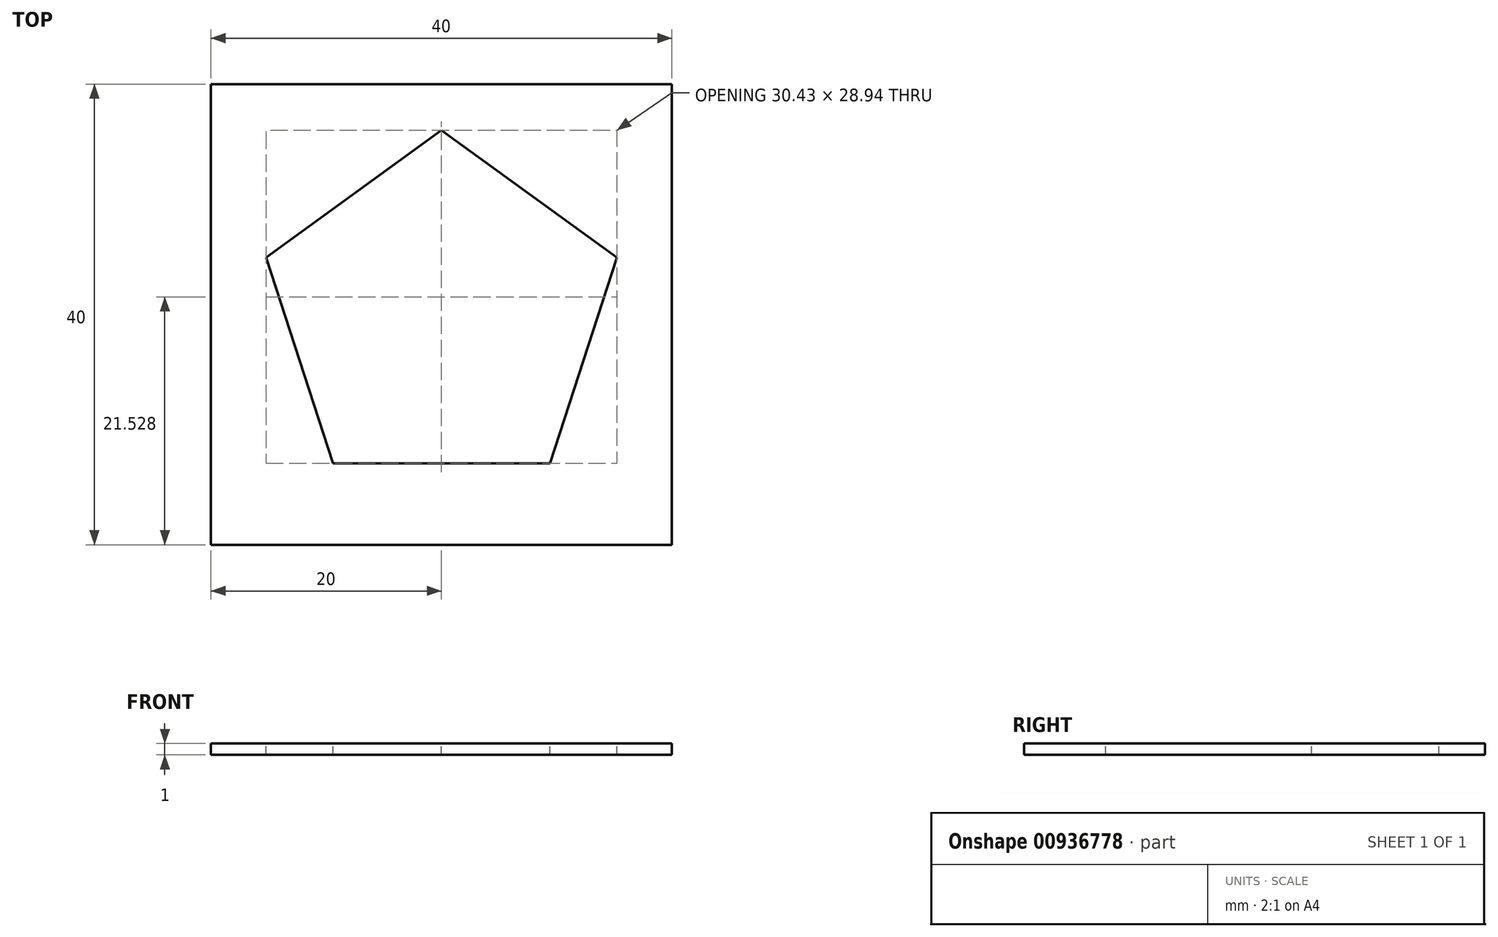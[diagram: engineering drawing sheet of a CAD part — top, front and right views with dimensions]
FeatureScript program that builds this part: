
annotation { "Feature Type Name" : "Feature", "Feature Type Description" : "" }
export const myFeature = defineFeature(function(context is Context, id is Id, definition is map)
    precondition{}
    {
        {
            var Q0;
            Q0=qCreatedBy(makeId("Top.planeOp"),FACE);
            var sketch = newSketch(context, id + "F0", { "sketchPlane" : qUnion([Q0])});
            skLineSegment(sketch, "E0.bottom", {"start": v(20, 20) * mm, "end": v(-20, 20) * mm});
            skLineSegment(sketch, "E0.top", {"start": v(20, -20) * mm, "end": v(-20, -20) * mm});
            skLineSegment(sketch, "E0.left", {"start": v(20, 20) * mm, "end": v(20, -20) * mm});
            skLineSegment(sketch, "E0.right", {"start": v(-20, 20) * mm, "end": v(-20, -20) * mm});
            skPoint(sketch, "E0.middle", {"position": v(0, 0) * mm});
            skSolve(sketch);
        }
        {
            var Q0;
            Q0 = qSketchRegion(id + "F0", true);
            extrude(context, id + "F1", {"entities" : qUnion([Q0]), "depth" : 1 * mm, "offsetDistance" : 25 * mm});
        }
        {
            var Q0;
            Q0=makeQuery(id+"F1.opExtrude","CAP_FACE",FACE,{"disambiguationData":[OSD([sQuery(id+"F0.wireOp",EDGE,"E0.bottom"),sQuery(id+"F0.wireOp",EDGE,"E0.top"),sQuery(id+"F0.wireOp",EDGE,"E0.left"),sQuery(id+"F0.wireOp",EDGE,"E0.right")])],"isStart":false});
            var sketch = newSketch(context, id + "F2", { "sketchPlane" : qUnion([Q0])});
            skCircle(sketch, "E1.cCircle", {"center": v(0, 0) * mm, "radius": 16 * mm, "construction": true});
            skLineSegment(sketch, "E1.0", {"start": v(-9.4, -12.94) * mm, "end": v(-15.22, 4.94) * mm});
            skLineSegment(sketch, "E1.1", {"start": v(-15.22, 4.94) * mm, "end": v(0, 16) * mm});
            skLineSegment(sketch, "E1.2", {"start": v(0, 16) * mm, "end": v(15.22, 4.94) * mm});
            skLineSegment(sketch, "E1.3", {"start": v(15.22, 4.94) * mm, "end": v(9.4, -12.94) * mm});
            skLineSegment(sketch, "E1.4", {"start": v(9.4, -12.94) * mm, "end": v(-9.4, -12.94) * mm});
            skSolve(sketch);
        }
        {
            var Q0;
            Q0 = qSketchRegion(id + "F2", true);
            extrude(context, id + "F3", {"entities" : qUnion([Q0]), "operationType" : NewBodyOperationType.REMOVE, "oppositeDirection" : true, "depth" : 25 * mm, "offsetDistance" : 25 * mm});
        }
    });
